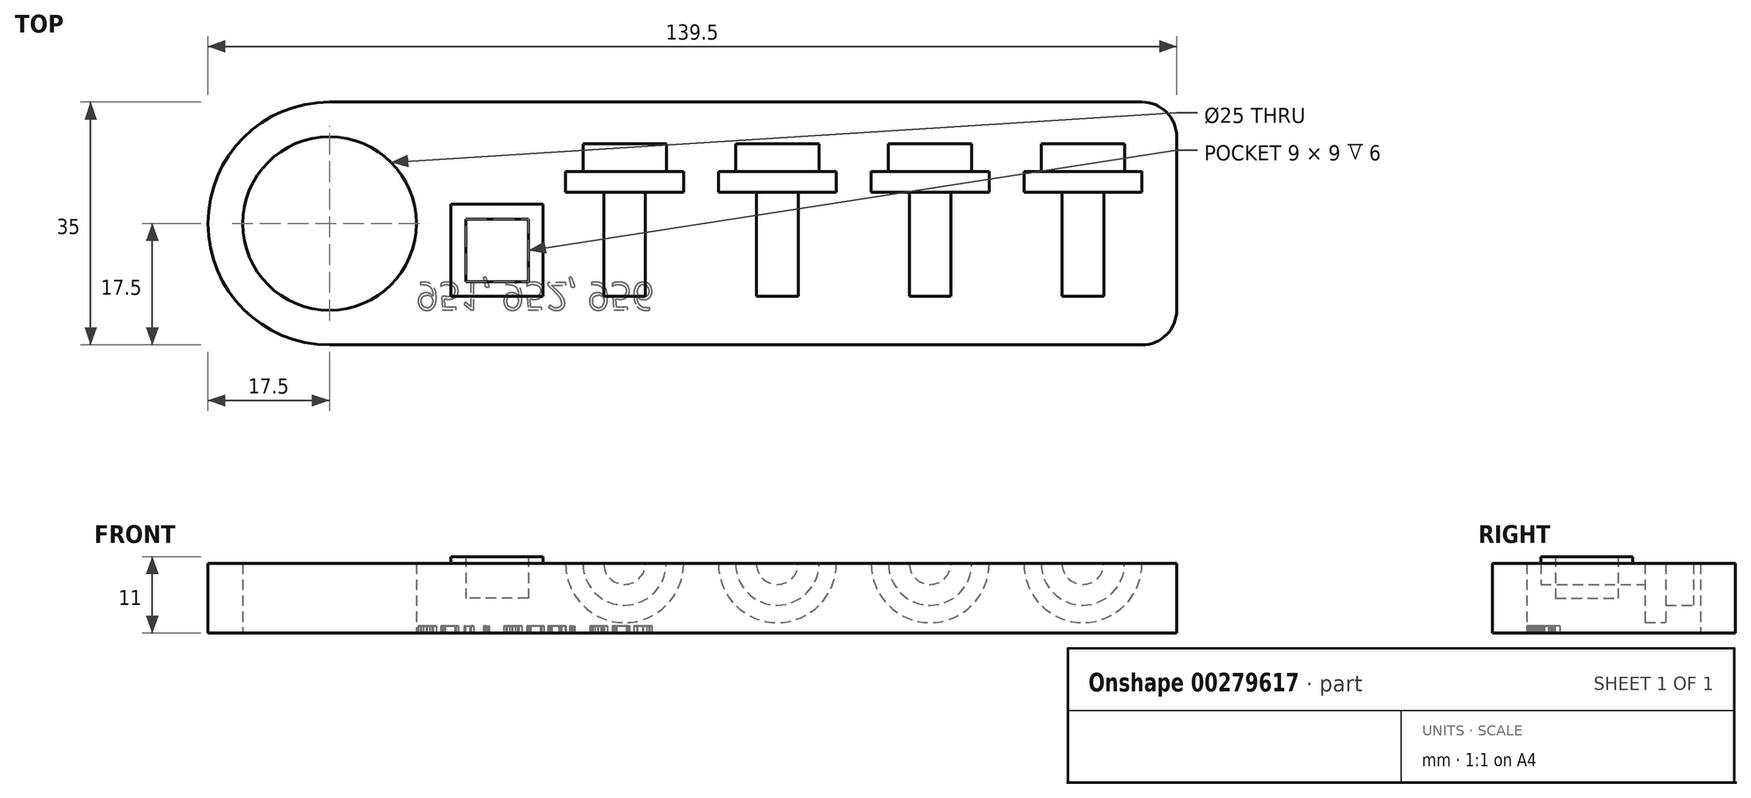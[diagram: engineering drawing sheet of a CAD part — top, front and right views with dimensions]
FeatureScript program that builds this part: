
annotation { "Feature Type Name" : "Feature", "Feature Type Description" : "" }
export const myFeature = defineFeature(function(context is Context, id is Id, definition is map)
    precondition{}
    {
        {
            var Q0;
            Q0=qCreatedBy(makeId("Top.planeOp"),FACE);
            var sketch = newSketch(context, id + "F0", { "sketchPlane" : qUnion([Q0])});
            skLineSegment(sketch, "E0.bottom", {"start": v(17.5, 0) * mm, "end": v(134.5, 0) * mm});
            skLineSegment(sketch, "E0.top", {"start": v(17.5, 35) * mm, "end": v(134.5, 35) * mm});
            skLineSegment(sketch, "E0.left", {"start": v(0, 17.5) * mm, "end": v(0, 17.5) * mm});
            skLineSegment(sketch, "E0.right", {"start": v(139.5, 5) * mm, "end": v(139.5, 30) * mm});
            skLineSegment(sketch, "E1.bottom", {"start": v(0, 0) * mm, "end": v(17.5, 0) * mm, "construction": true});
            skLineSegment(sketch, "E1.top", {"start": v(0, 17.5) * mm, "end": v(17.5, 17.5) * mm, "construction": true});
            skLineSegment(sketch, "E1.left", {"start": v(0, 0) * mm, "end": v(0, 17.5) * mm, "construction": true});
            skLineSegment(sketch, "E1.right", {"start": v(17.5, 0) * mm, "end": v(17.5, 17.5) * mm, "construction": true});
            skCircle(sketch, "E2", {"center": v(17.5, 17.5) * mm, "radius": 12.5 * mm});
            skPoint(sketch, "E3.visualSharp", {"position": v(0, 0) * mm});
            skArc(sketch, "E3.filletArc", {"start": v(0, 17.5) * mm, "mid": v(5.13, 5.13) * mm, "end": v(17.5, 0) * mm});
            skPoint(sketch, "E4.visualSharp", {"position": v(0, 35) * mm});
            skArc(sketch, "E4.filletArc", {"start": v(17.5, 35) * mm, "mid": v(5.13, 29.87) * mm, "end": v(0, 17.5) * mm});
            skPoint(sketch, "E5.visualSharp", {"position": v(139.5, 35) * mm});
            skArc(sketch, "E5.filletArc", {"start": v(139.5, 30) * mm, "mid": v(138.04, 33.54) * mm, "end": v(134.5, 35) * mm});
            skPoint(sketch, "E6.visualSharp", {"position": v(139.5, 0) * mm});
            skArc(sketch, "E6.filletArc", {"start": v(134.5, 0) * mm, "mid": v(138.04, 1.46) * mm, "end": v(139.5, 5) * mm});
            skSolve(sketch);
        }
        {
            var Q0;
            Q0=makeQuery(id+"F0.imprint","IMPRINT",FACE,{"disambiguationData":[TD([[makeQuery(id+"F0.imprint","IMPRINT",EDGE,{"derivedFrom":sQuery(id+"F0.wireOp",EDGE,"E0.bottom")}),1.0]])]});
            extrude(context, id + "F1", {"entities" : qUnion([Q0]), "depth" : 10 * mm});
        }
        {
            var Q0;
            Q0=makeQuery(id+"F1.opExtrude","CAP_FACE",FACE,{"disambiguationData":[OSD([sQuery(id+"F0.wireOp",EDGE,"E0.bottom"),sQuery(id+"F0.wireOp",EDGE,"E0.top"),sQuery(id+"F0.wireOp",EDGE,"E0.right"),sQuery(id+"F0.wireOp",EDGE,"E2"),sQuery(id+"F0.wireOp",EDGE,"E3.filletArc"),sQuery(id+"F0.wireOp",EDGE,"E4.filletArc"),sQuery(id+"F0.wireOp",EDGE,"E5.filletArc"),sQuery(id+"F0.wireOp",EDGE,"E6.filletArc")])],"isStart":false});
            var sketch = newSketch(context, id + "F2", { "sketchPlane" : qUnion([Q0])});
            skLineSegment(sketch, "E7.bottom", {"start": v(0, 0) * mm, "end": v(60, 0) * mm, "construction": true});
            skLineSegment(sketch, "E7.top", {"start": v(0, 7) * mm, "end": v(60, 7) * mm, "construction": true});
            skLineSegment(sketch, "E7.left", {"start": v(0, 0) * mm, "end": v(0, 7) * mm, "construction": true});
            skLineSegment(sketch, "E7.right", {"start": v(60, 0) * mm, "end": v(60, 7) * mm, "construction": true});
            skLineSegment(sketch, "E8.bottom", {"start": v(60, 7) * mm, "end": v(63, 7) * mm});
            skLineSegment(sketch, "E8.left", {"start": v(60, 7) * mm, "end": v(60, 22) * mm});
            skLineSegment(sketch, "E8.right", {"start": v(63, 7) * mm, "end": v(63, 22) * mm});
            skLineSegment(sketch, "E9.bottom", {"start": v(63, 22) * mm, "end": v(68.5, 22) * mm});
            skLineSegment(sketch, "E9.top", {"start": v(66, 25) * mm, "end": v(68.5, 25) * mm});
            skLineSegment(sketch, "E9.left", {"start": v(60, 22) * mm, "end": v(60, 25) * mm});
            skLineSegment(sketch, "E9.right", {"start": v(68.5, 22) * mm, "end": v(68.5, 25) * mm});
            skLineSegment(sketch, "E10.top", {"start": v(60, 29) * mm, "end": v(66, 29) * mm});
            skLineSegment(sketch, "E10.left", {"start": v(60, 25) * mm, "end": v(60, 29) * mm});
            skLineSegment(sketch, "E10.right", {"start": v(66, 25) * mm, "end": v(66, 29) * mm});
            skLineSegment(sketch, "E11", {"start": v(60, 7) * mm, "end": v(82, 7) * mm, "construction": true});
            skLineSegment(sketch, "E12", {"start": v(82, 7) * mm, "end": v(104, 7) * mm, "construction": true});
            skLineSegment(sketch, "E13", {"start": v(104, 7) * mm, "end": v(126, 7) * mm, "construction": true});
            skLineSegment(sketch, "E14.bottom", {"start": v(82, 7) * mm, "end": v(85, 7) * mm});
            skLineSegment(sketch, "E14.left", {"start": v(82, 7) * mm, "end": v(82, 22) * mm});
            skLineSegment(sketch, "E14.right", {"start": v(85, 7) * mm, "end": v(85, 22) * mm});
            skLineSegment(sketch, "E15.bottom", {"start": v(85, 22) * mm, "end": v(90.5, 22) * mm});
            skLineSegment(sketch, "E15.top", {"start": v(88, 25) * mm, "end": v(90.5, 25) * mm});
            skLineSegment(sketch, "E15.left", {"start": v(82, 22) * mm, "end": v(82, 25) * mm});
            skLineSegment(sketch, "E15.right", {"start": v(90.5, 22) * mm, "end": v(90.5, 25) * mm});
            skLineSegment(sketch, "E16.top", {"start": v(82, 29) * mm, "end": v(88, 29) * mm});
            skLineSegment(sketch, "E16.left", {"start": v(82, 25) * mm, "end": v(82, 29) * mm});
            skLineSegment(sketch, "E16.right", {"start": v(88, 25) * mm, "end": v(88, 29) * mm});
            skLineSegment(sketch, "E17.bottom", {"start": v(104, 7) * mm, "end": v(107, 7) * mm});
            skLineSegment(sketch, "E17.left", {"start": v(104, 7) * mm, "end": v(104, 22) * mm});
            skLineSegment(sketch, "E17.right", {"start": v(107, 7) * mm, "end": v(107, 22) * mm});
            skLineSegment(sketch, "E18.bottom", {"start": v(107, 22) * mm, "end": v(112.5, 22) * mm});
            skLineSegment(sketch, "E18.top", {"start": v(110, 25) * mm, "end": v(112.5, 25) * mm});
            skLineSegment(sketch, "E18.left", {"start": v(104, 22) * mm, "end": v(104, 25) * mm});
            skLineSegment(sketch, "E18.right", {"start": v(112.5, 22) * mm, "end": v(112.5, 25) * mm});
            skLineSegment(sketch, "E19.top", {"start": v(104, 29) * mm, "end": v(110, 29) * mm});
            skLineSegment(sketch, "E19.left", {"start": v(104, 25) * mm, "end": v(104, 29) * mm});
            skLineSegment(sketch, "E19.right", {"start": v(110, 25) * mm, "end": v(110, 29) * mm});
            skLineSegment(sketch, "E20.bottom", {"start": v(126, 7) * mm, "end": v(129, 7) * mm});
            skLineSegment(sketch, "E20.left", {"start": v(126, 7) * mm, "end": v(126, 22) * mm});
            skLineSegment(sketch, "E20.right", {"start": v(129, 7) * mm, "end": v(129, 22) * mm});
            skLineSegment(sketch, "E21.bottom", {"start": v(129, 22) * mm, "end": v(134.5, 22) * mm});
            skLineSegment(sketch, "E21.top", {"start": v(132, 25) * mm, "end": v(134.5, 25) * mm});
            skLineSegment(sketch, "E21.left", {"start": v(126, 22) * mm, "end": v(126, 25) * mm});
            skLineSegment(sketch, "E21.right", {"start": v(134.5, 22) * mm, "end": v(134.5, 25) * mm});
            skLineSegment(sketch, "E22.top", {"start": v(126, 29) * mm, "end": v(132, 29) * mm});
            skLineSegment(sketch, "E22.left", {"start": v(126, 25) * mm, "end": v(126, 29) * mm});
            skLineSegment(sketch, "E22.right", {"start": v(132, 25) * mm, "end": v(132, 29) * mm});
            skLineSegment(sketch, "E23", {"start": v(0, 7) * mm, "end": v(35, 7) * mm, "construction": true});
            skLineSegment(sketch, "E24.bottom", {"start": v(48.25, 7) * mm, "end": v(35, 7) * mm});
            skLineSegment(sketch, "E24.top", {"start": v(48.25, 20.25) * mm, "end": v(35, 20.25) * mm});
            skLineSegment(sketch, "E24.left", {"start": v(48.25, 7) * mm, "end": v(48.25, 20.25) * mm});
            skLineSegment(sketch, "E24.right", {"start": v(35, 7) * mm, "end": v(35, 20.25) * mm});
            skPoint(sketch, "E24.middle", {"position": v(41.62, 13.63) * mm});
            skLineSegment(sketch, "E25.bottom", {"start": v(46.12, 9.13) * mm, "end": v(37.12, 9.13) * mm});
            skLineSegment(sketch, "E25.top", {"start": v(46.12, 18.13) * mm, "end": v(37.12, 18.13) * mm});
            skLineSegment(sketch, "E25.left", {"start": v(46.12, 9.13) * mm, "end": v(46.12, 18.13) * mm});
            skLineSegment(sketch, "E25.right", {"start": v(37.12, 9.13) * mm, "end": v(37.12, 18.13) * mm});
            skSolve(sketch);
        }
        {
            var Q0;
            Q0=makeQuery(id+"F2.imprint","IMPRINT",FACE,{"disambiguationData":[TD([[makeQuery(id+"F2.imprint","IMPRINT",EDGE,{"derivedFrom":sQuery(id+"F2.wireOp",EDGE,"E8.bottom")}),1.0]])]});
            var Q1;
            Q1=sQuery(id+"F2.wireOp",EDGE,"E8.left");
            revolve(context, id + "F3", {"operationType" : NewBodyOperationType.REMOVE, "entities" : qUnion([Q0]), "axis" : qUnion([Q1]), "revolveType" : RevolveType.FULL, "oppositeDirection" : true});
        }
        {
            var Q0;
            Q0=makeQuery(id+"F2.imprint","IMPRINT",FACE,{"disambiguationData":[TD([[makeQuery(id+"F2.imprint","IMPRINT",EDGE,{"derivedFrom":sQuery(id+"F2.wireOp",EDGE,"E14.bottom")}),1.0]])]});
            var Q1;
            Q1=sQuery(id+"F2.wireOp",EDGE,"E14.left");
            revolve(context, id + "F4", {"operationType" : NewBodyOperationType.REMOVE, "entities" : qUnion([Q0]), "axis" : qUnion([Q1]), "revolveType" : RevolveType.FULL, "oppositeDirection" : true});
        }
        {
            var Q0;
            Q0=makeQuery(id+"F2.imprint","IMPRINT",FACE,{"disambiguationData":[TD([[makeQuery(id+"F2.imprint","IMPRINT",EDGE,{"derivedFrom":sQuery(id+"F2.wireOp",EDGE,"E17.bottom")}),1.0]])]});
            var Q1;
            Q1=sQuery(id+"F2.wireOp",EDGE,"E17.left");
            revolve(context, id + "F5", {"operationType" : NewBodyOperationType.REMOVE, "entities" : qUnion([Q0]), "axis" : qUnion([Q1]), "revolveType" : RevolveType.FULL, "oppositeDirection" : true});
        }
        {
            var Q0;
            Q0=makeQuery(id+"F2.imprint","IMPRINT",FACE,{"disambiguationData":[TD([[makeQuery(id+"F2.imprint","IMPRINT",EDGE,{"derivedFrom":sQuery(id+"F2.wireOp",EDGE,"E20.bottom")}),1.0]])]});
            var Q1;
            Q1=sQuery(id+"F2.wireOp",EDGE,"E20.left");
            revolve(context, id + "F6", {"operationType" : NewBodyOperationType.REMOVE, "entities" : qUnion([Q0]), "axis" : qUnion([Q1]), "revolveType" : RevolveType.FULL, "oppositeDirection" : true});
        }
        {
            var Q0;
            Q0=makeQuery(id+"F2.imprint","IMPRINT",FACE,{"disambiguationData":[TD([[makeQuery(id+"F2.imprint","IMPRINT",EDGE,{"derivedFrom":sQuery(id+"F2.wireOp",EDGE,"E24.bottom")}),-1.0]])]});
            extrude(context, id + "F7", {"entities" : qUnion([Q0]), "operationType" : NewBodyOperationType.ADD, "depth" : 1 * mm});
        }
        {
            var Q0;
            Q0=makeQuery(id+"F2.imprint","IMPRINT",FACE,{"disambiguationData":[TD([[makeQuery(id+"F2.imprint","IMPRINT",EDGE,{"derivedFrom":sQuery(id+"F2.wireOp",EDGE,"E25.bottom")}),-1.0]])]});
            extrude(context, id + "F8", {"entities" : qUnion([Q0]), "operationType" : NewBodyOperationType.REMOVE, "oppositeDirection" : true, "depth" : 5 * mm});
        }
        {
            var Q0;
            Q0=makeQuery(id+"F1.opExtrude","CAP_FACE",FACE,{"disambiguationData":[OSD([sQuery(id+"F0.wireOp",EDGE,"E0.bottom"),sQuery(id+"F0.wireOp",EDGE,"E0.top"),sQuery(id+"F0.wireOp",EDGE,"E0.right"),sQuery(id+"F0.wireOp",EDGE,"E2"),sQuery(id+"F0.wireOp",EDGE,"E3.filletArc"),sQuery(id+"F0.wireOp",EDGE,"E4.filletArc"),sQuery(id+"F0.wireOp",EDGE,"E5.filletArc"),sQuery(id+"F0.wireOp",EDGE,"E6.filletArc")])],"isStart":true});
            var sketch = newSketch(context, id + "F9", { "sketchPlane" : qUnion([Q0])});
            skLineSegment(sketch, "E26.bottom", {"start": v(0, 0) * mm, "end": v(30, 0) * mm, "construction": true});
            skLineSegment(sketch, "E26.top", {"start": v(0, -5) * mm, "end": v(30, -5) * mm, "construction": true});
            skLineSegment(sketch, "E26.left", {"start": v(0, 0) * mm, "end": v(0, -5) * mm, "construction": true});
            skLineSegment(sketch, "E26.right", {"start": v(30, 0) * mm, "end": v(30, -5) * mm, "construction": true});
            skText(sketch, "E27", { "text": "951, 952, 956\n", "fontName": "OpenSans-Regular.ttf"});
            const initialGuessF9  = {"E27": [0.03, -0.009, 1, 0, 0.004]};
            skSetInitialGuess(sketch, initialGuessF9);
            skSolve(sketch);
        }
        {
            var Q0;
            Q0 = qSketchRegion(id + "F9", true);
            extrude(context, id + "F10", {"entities" : qUnion([Q0]), "operationType" : NewBodyOperationType.REMOVE, "oppositeDirection" : true, "depth" : 1 * mm});
        }
    });
